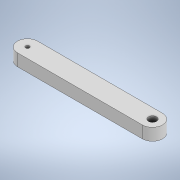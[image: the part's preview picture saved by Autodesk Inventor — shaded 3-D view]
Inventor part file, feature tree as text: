
AUTODESK INVENTOR PART (.ipt)
format: ipt  version: 2020 (Build 240168000, 168)  size: 104,960 bytes
history: native  units: in
note: dims shown in document units (in); Inventor stores cm internally (conversion verified against a paired STEP export)
features: extrude x1, sketch x1
ambient origin geometry x8: Origin, YZ Plane, XZ Plane, XY Plane, X Axis, Y Axis, Z Axis, Center Point
bodies: Solid1 (feature_tree)
feature tree (2):
  extrude  "Extrusion1"  Depth=0.0984in
  sketch  "Sketch1"  dims[d0=0.1969in d1=0.0984in d2=1.2205in d3=0.0374in d4=0.0787in d5=0.1181in d6=0.0in]
